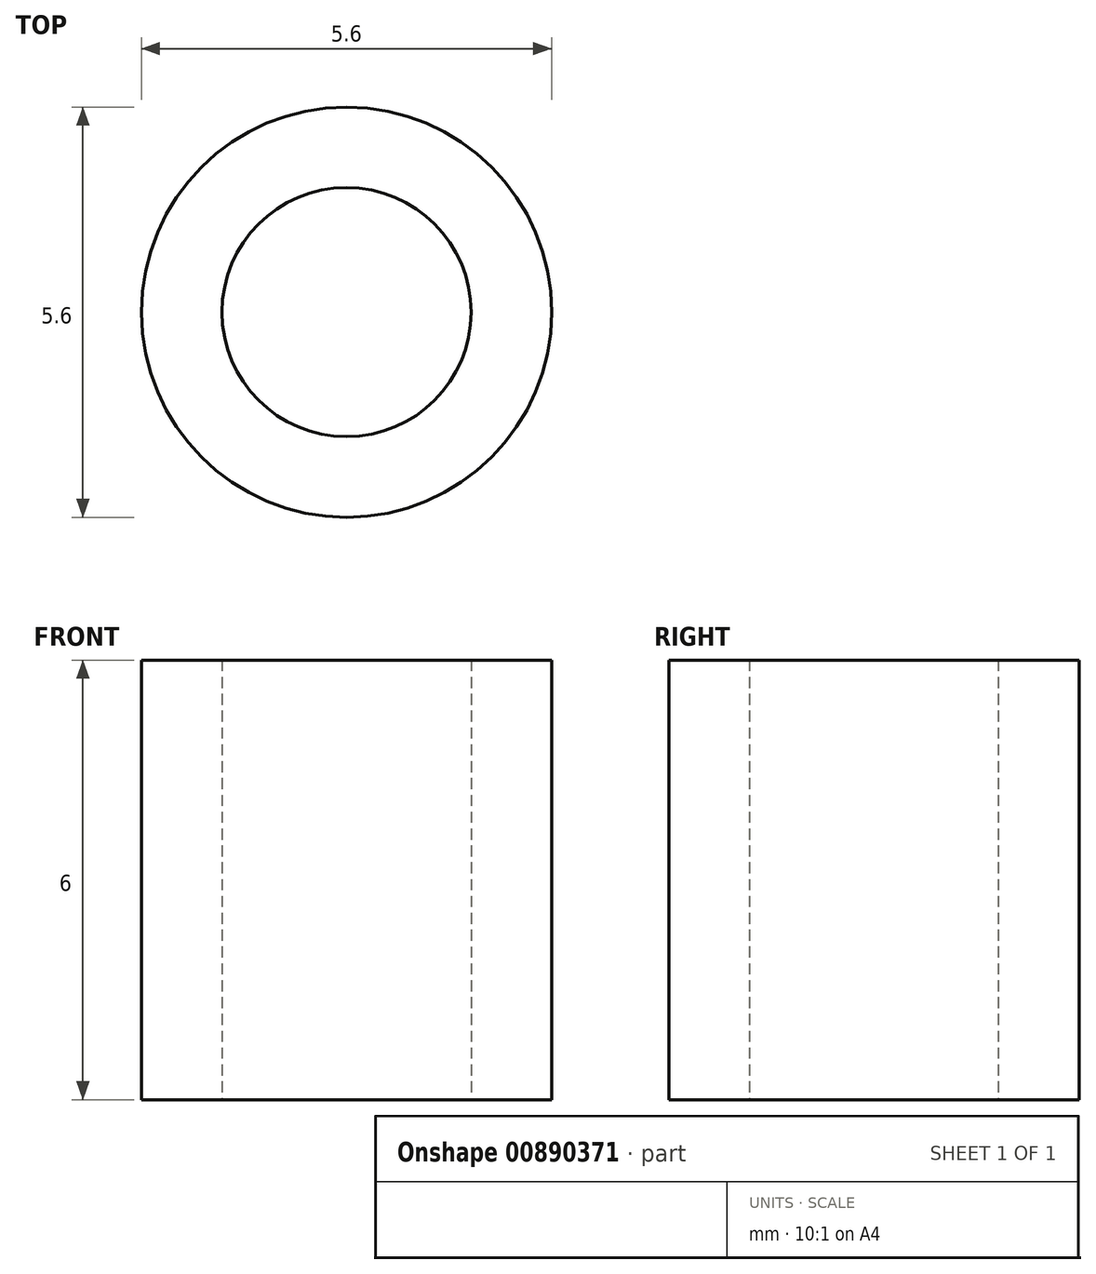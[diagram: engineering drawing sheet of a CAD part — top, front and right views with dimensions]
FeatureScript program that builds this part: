
annotation { "Feature Type Name" : "Feature", "Feature Type Description" : "" }
export const myFeature = defineFeature(function(context is Context, id is Id, definition is map)
    precondition{}
    {
        {
            var Q0;
            Q0=qCreatedBy(makeId("Top.planeOp"),FACE);
            var sketch = newSketch(context, id + "F0", { "sketchPlane" : qUnion([Q0])});
            skCircle(sketch, "E0", {"center": v(0, 0) * mm, "radius": 2.8 * mm});
            skCircle(sketch, "E1", {"center": v(0, 0) * mm, "radius": 1.7 * mm});
            skSolve(sketch);
        }
        {
            var Q0;
            Q0=makeQuery(id+"F0.imprint","IMPRINT",FACE,{"disambiguationData":[TD([[makeQuery(id+"F0.imprint","IMPRINT",EDGE,{"derivedFrom":sQuery(id+"F0.wireOp",EDGE,"E0")}),1.0]])]});
            extrude(context, id + "F1", {"entities" : qUnion([Q0]), "depth" : 6 * mm, "offsetDistance" : 25 * mm});
        }
    });
